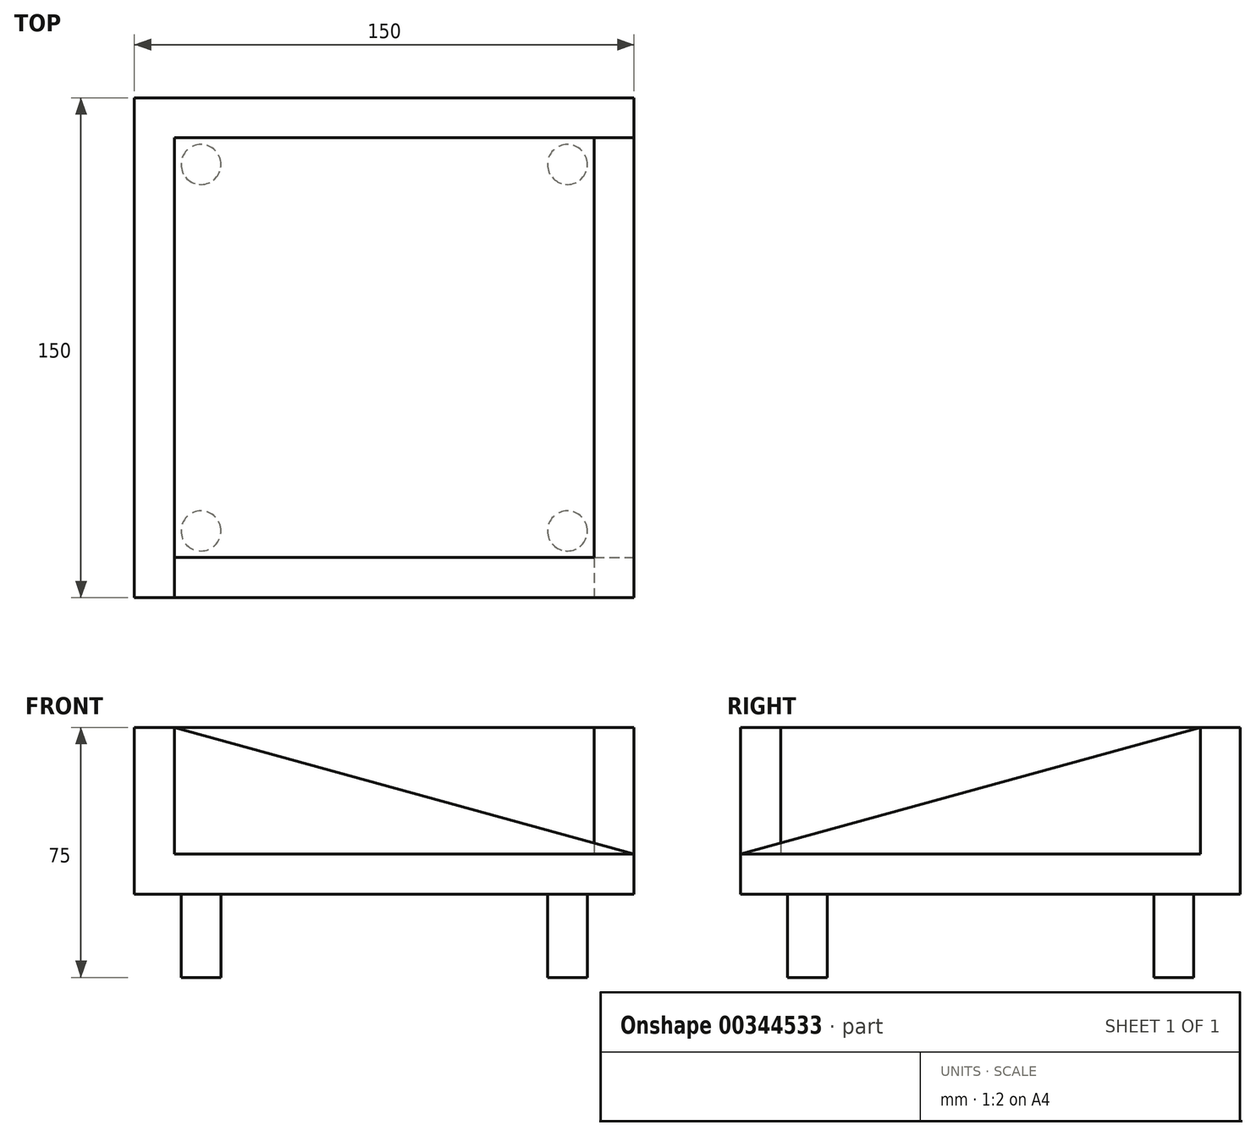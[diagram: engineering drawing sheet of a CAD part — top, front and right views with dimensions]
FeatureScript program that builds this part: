
annotation { "Feature Type Name" : "Feature", "Feature Type Description" : "" }
export const myFeature = defineFeature(function(context is Context, id is Id, definition is map)
    precondition{}
    {
        {
            var Q0;
            Q0=qCreatedBy(makeId("Top.planeOp"),FACE);
            var sketch = newSketch(context, id + "F0", { "sketchPlane" : qUnion([Q0])});
            skLineSegment(sketch, "E0.bottom", {"start": v(-75, 75) * mm, "end": v(75, 75) * mm});
            skLineSegment(sketch, "E0.top", {"start": v(-75, -75) * mm, "end": v(75, -75) * mm});
            skLineSegment(sketch, "E0.left", {"start": v(-75, 75) * mm, "end": v(-75, -75) * mm});
            skLineSegment(sketch, "E0.right", {"start": v(75, 75) * mm, "end": v(75, -75) * mm});
            skPoint(sketch, "E0.middle", {"position": v(0, 0) * mm});
            skSolve(sketch);
        }
        {
            var Q0;
            Q0=makeQuery(id+"F0.imprint","IMPRINT",FACE,{"disambiguationData":[TD([[makeQuery(id+"F0.imprint","IMPRINT",EDGE,{"derivedFrom":sQuery(id+"F0.wireOp",EDGE,"E0.bottom")}),-1.0]])]});
            extrude(context, id + "F1", {"entities" : qUnion([Q0]), "oppositeDirection" : true, "depth" : 12 * mm});
        }
        {
            var Q0;
            Q0=makeQuery(id+"F1.opExtrude","CAP_FACE",FACE,{"disambiguationData":[OSD([sQuery(id+"F0.wireOp",EDGE,"E0.bottom"),sQuery(id+"F0.wireOp",EDGE,"E0.top"),sQuery(id+"F0.wireOp",EDGE,"E0.left"),sQuery(id+"F0.wireOp",EDGE,"E0.right")])],"isStart":true});
            var sketch = newSketch(context, id + "F2", { "sketchPlane" : qUnion([Q0])});
            skLineSegment(sketch, "E1.bottom", {"start": v(-75, 75) * mm, "end": v(75, 75) * mm});
            skLineSegment(sketch, "E1.top", {"start": v(-75, 63) * mm, "end": v(75, 63) * mm});
            skLineSegment(sketch, "E1.left", {"start": v(-75, 75) * mm, "end": v(-75, 63) * mm});
            skLineSegment(sketch, "E1.right", {"start": v(75, 75) * mm, "end": v(75, 63) * mm});
            skLineSegment(sketch, "E2.bottom", {"start": v(-75, 75) * mm, "end": v(-63, 75) * mm});
            skLineSegment(sketch, "E2.top", {"start": v(-75, -75) * mm, "end": v(-63, -75) * mm});
            skLineSegment(sketch, "E2.left", {"start": v(-75, 75) * mm, "end": v(-75, -75) * mm});
            skLineSegment(sketch, "E2.right", {"start": v(-63, 75) * mm, "end": v(-63, -75) * mm});
            skSolve(sketch);
        }
        {
            var Q0;
            {var subQ5=sQuery(id+"F2.wireOp",EDGE,"E2.top");Q0=makeQuery(id+"F2.imprint","IMPRINT",FACE,{"disambiguationData":[TD([[makeQuery(id+"F2.imprint","IMPRINT",EDGE,{"derivedFrom":subQ5}),1.0]])]});}
            var Q1;
            {var subQ5=sQuery(id+"F2.wireOp",EDGE,"E2.bottom");Q1=makeQuery(id+"F2.imprint","IMPRINT",FACE,{"disambiguationData":[TD([[makeQuery(id+"F2.imprint","IMPRINT",EDGE,{"derivedFrom":subQ5}),-1.0]])]});}
            var Q2;
            {var subQ0=sQuery(id+"F2.wireOp",EDGE,"E1.bottom");Q2=makeQuery(id+"F2.imprint","IMPRINT",FACE,{"disambiguationData":[TD([[makeQuery(id+"F2.imprint","IMPRINT",EDGE,{"derivedFrom":subQ0}),-1.0]])]});}
            extrude(context, id + "F3", {"entities" : qUnion([Q0, Q1, Q2]), "operationType" : NewBodyOperationType.ADD, "depth" : 38 * mm});
        }
        {
            var Q0;
            Q0=makeQuery(id+"F3.boolean.opBoolean","MERGE",FACE,{"derivedFrom":[makeQuery(id+"F1.opExtrude","SWEPT_FACE",FACE,{"disambiguationData":[OSD([sQuery(id+"F0.wireOp",EDGE,"E0.top")])]}),makeQuery(id+"F3.opExtrude","SWEPT_FACE",FACE,{"disambiguationData":[OSD([sQuery(id+"F2.wireOp",EDGE,"E2.top")])]})]});
            var sketch = newSketch(context, id + "F4", { "sketchPlane" : qUnion([Q0])});
            skLineSegment(sketch, "E3", {"start": v(-63, 38) * mm, "end": v(75, 0) * mm});
            skSolve(sketch);
        }
        {
            var Q0;
            Q0=makeQuery(id+"F4.imprint","IMPRINT",FACE,{"disambiguationData":[TD([[makeQuery(id+"F4.imprint","IMPRINT",EDGE,{"derivedFrom":sQuery(id+"F4.wireOp",EDGE,"E3")}),-1.0]])]});
            extrude(context, id + "F5", {"entities" : qUnion([Q0]), "oppositeDirection" : true, "depth" : 12 * mm});
        }
        {
            var Q0;
            Q0=makeQuery(id+"F3.boolean.opBoolean","MERGE",FACE,{"derivedFrom":[makeQuery(id+"F1.opExtrude","SWEPT_FACE",FACE,{"disambiguationData":[OSD([sQuery(id+"F0.wireOp",EDGE,"E0.right")])]}),makeQuery(id+"F3.opExtrude","SWEPT_FACE",FACE,{"disambiguationData":[OSD([sQuery(id+"F2.wireOp",EDGE,"E1.right")])]})]});
            var sketch = newSketch(context, id + "F6", { "sketchPlane" : qUnion([Q0])});
            skLineSegment(sketch, "E4", {"start": v(63, 38) * mm, "end": v(-75, 0) * mm});
            skSolve(sketch);
        }
        {
            var Q0;
            Q0=makeQuery(id+"F6.imprint","IMPRINT",FACE,{"disambiguationData":[TD([[makeQuery(id+"F6.imprint","IMPRINT",EDGE,{"derivedFrom":sQuery(id+"F6.wireOp",EDGE,"E4")}),1.0]])]});
            extrude(context, id + "F7", {"entities" : qUnion([Q0]), "oppositeDirection" : true, "depth" : 12 * mm});
        }
        {
            var Q0;
            Q0=makeQuery(id+"F1.opExtrude","CAP_FACE",FACE,{"disambiguationData":[OSD([sQuery(id+"F0.wireOp",EDGE,"E0.bottom"),sQuery(id+"F0.wireOp",EDGE,"E0.top"),sQuery(id+"F0.wireOp",EDGE,"E0.left"),sQuery(id+"F0.wireOp",EDGE,"E0.right")])],"isStart":false});
            var sketch = newSketch(context, id + "F8", { "sketchPlane" : qUnion([Q0])});
            skPoint(sketch, "E5.middle", {"position": v(0, 0) * mm});
            skCircle(sketch, "E6", {"center": v(-55, 55) * mm, "radius": 6 * mm});
            skCircle(sketch, "E7", {"center": v(55, 55) * mm, "radius": 6 * mm});
            skCircle(sketch, "E8", {"center": v(-55, -55) * mm, "radius": 6 * mm});
            skCircle(sketch, "E9", {"center": v(55, -55) * mm, "radius": 6 * mm});
            skSolve(sketch);
        }
        {
            var Q0;
            Q0=makeQuery(id+"F8.imprint","IMPRINT",FACE,{"disambiguationData":[TD([[makeQuery(id+"F8.imprint","IMPRINT",EDGE,{"derivedFrom":sQuery(id+"F8.wireOp",EDGE,"E6")}),1.0]])]});
            var Q1;
            Q1=makeQuery(id+"F8.imprint","IMPRINT",FACE,{"disambiguationData":[TD([[makeQuery(id+"F8.imprint","IMPRINT",EDGE,{"derivedFrom":sQuery(id+"F8.wireOp",EDGE,"E7")}),1.0]])]});
            var Q2;
            Q2=makeQuery(id+"F8.imprint","IMPRINT",FACE,{"disambiguationData":[TD([[makeQuery(id+"F8.imprint","IMPRINT",EDGE,{"derivedFrom":sQuery(id+"F8.wireOp",EDGE,"E9")}),1.0]])]});
            var Q3;
            Q3=makeQuery(id+"F8.imprint","IMPRINT",FACE,{"disambiguationData":[TD([[makeQuery(id+"F8.imprint","IMPRINT",EDGE,{"derivedFrom":sQuery(id+"F8.wireOp",EDGE,"E8")}),1.0]])]});
            extrude(context, id + "F9", {"entities" : qUnion([Q0, Q1, Q2, Q3]), "operationType" : NewBodyOperationType.ADD, "depth" : 25 * mm});
        }
    });
